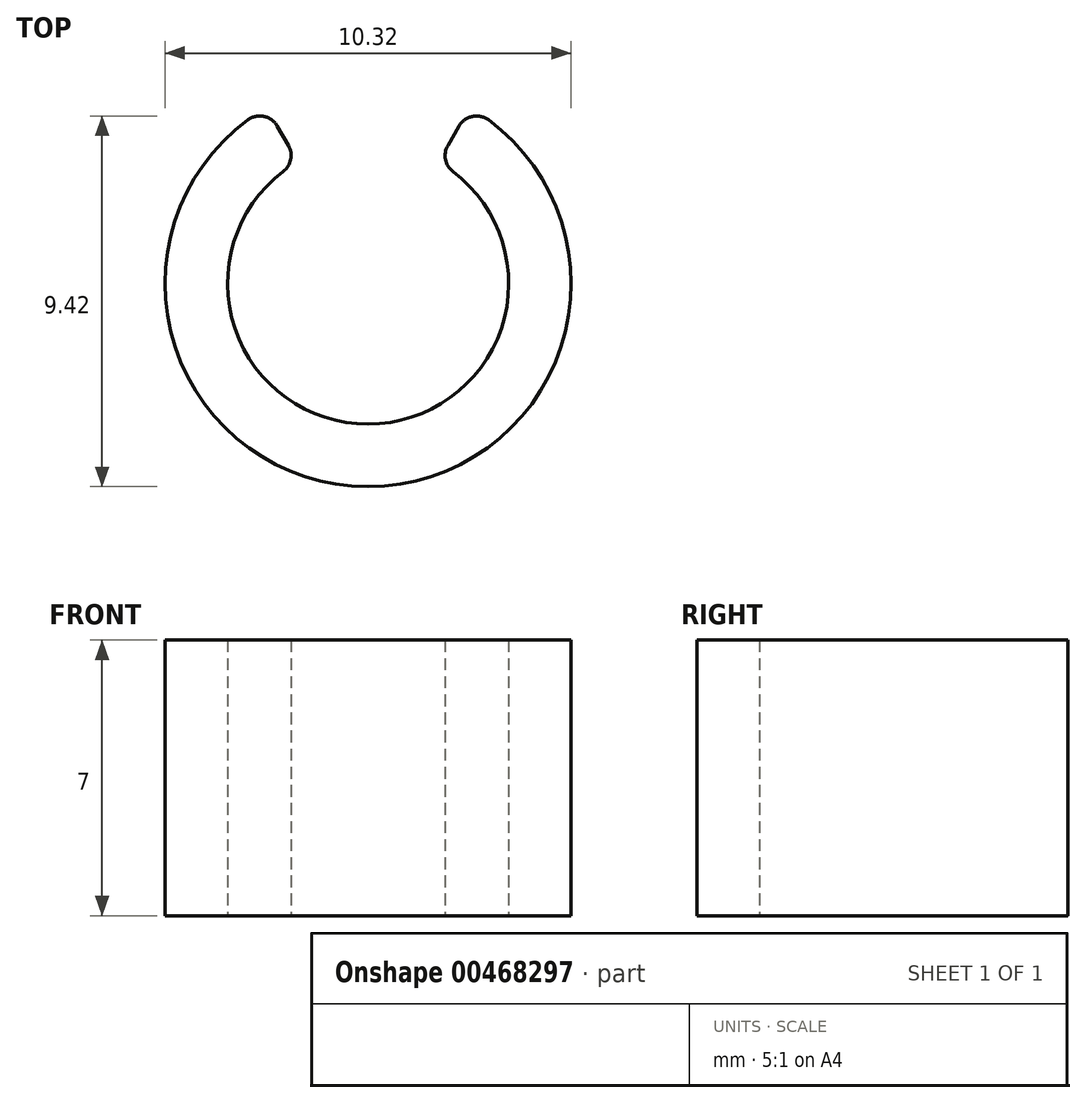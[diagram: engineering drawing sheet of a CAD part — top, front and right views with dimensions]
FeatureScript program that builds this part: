
annotation { "Feature Type Name" : "Feature", "Feature Type Description" : "" }
export const myFeature = defineFeature(function(context is Context, id is Id, definition is map)
    precondition{}
    {
        {
            var Q0;
            Q0=qCreatedBy(makeId("Top.planeOp"),FACE);
            var sketch = newSketch(context, id + "F0", { "sketchPlane" : qUnion([Q0])});
            skCircle(sketch, "E0", {"center": v(0, 0) * mm, "radius": 3.57 * mm});
            skCircle(sketch, "E1", {"center": v(0, 0) * mm, "radius": 5.16 * mm});
            skSolve(sketch);
        }
        {
            var Q0;
            Q0 = qSketchRegion(id + "F0", true);
            extrude(context, id + "F1", {"entities" : qUnion([Q0]), "depth" : 7 * mm});
        }
        {
            var Q0;
            Q0=qCreatedBy(makeId("Top.planeOp"),FACE);
            var sketch = newSketch(context, id + "F2", { "sketchPlane" : qUnion([Q0])});
            skCircle(sketch, "E2.cCircle", {"center": v(0, 3.44) * mm, "radius": 1.72 * mm, "construction": true});
            skLineSegment(sketch, "E2.0", {"start": v(0, 0) * mm, "end": v(-2.98, 5.16) * mm});
            skLineSegment(sketch, "E2.1", {"start": v(-2.98, 5.16) * mm, "end": v(2.98, 5.16) * mm});
            skLineSegment(sketch, "E2.2", {"start": v(2.98, 5.16) * mm, "end": v(0, 0) * mm});
            skPoint(sketch, "E2.0.midPoint", {"position": v(-1.49, 2.58) * mm});
            skSolve(sketch);
        }
        {
            var Q0;
            Q0 = qSketchRegion(id + "F2", true);
            extrude(context, id + "F3", {"entities" : qUnion([Q0]), "operationType" : NewBodyOperationType.REMOVE, "endBound" : BoundingType.THROUGH_ALL, "depth" : 25.4 * mm});
        }
        {
            var Q0;
            Q0=makeQuery(id+"F3.boolean.opBoolean","INTERSECT",EDGE,{"derivedFrom":[makeQuery(id+"F1.opExtrude","SWEPT_FACE",FACE,{"disambiguationData":[OSD([sQuery(id+"F0.wireOp",EDGE,"E0")])]}),makeQuery(id+"F3.opExtrude","SWEPT_FACE",FACE,{"disambiguationData":[OSD([sQuery(id+"F2.wireOp",EDGE,"E2.2")])]})]});
            var Q1;
            Q1=makeQuery(id+"F3.boolean.opBoolean","INTERSECT",EDGE,{"derivedFrom":[makeQuery(id+"F1.opExtrude","SWEPT_FACE",FACE,{"disambiguationData":[OSD([sQuery(id+"F0.wireOp",EDGE,"E0")])]}),makeQuery(id+"F3.opExtrude","SWEPT_FACE",FACE,{"disambiguationData":[OSD([sQuery(id+"F2.wireOp",EDGE,"E2.0")])]})]});
            var Q2;
            Q2=makeQuery(id+"F3.boolean.opBoolean","INTERSECT",EDGE,{"derivedFrom":[makeQuery(id+"F1.opExtrude","SWEPT_FACE",FACE,{"disambiguationData":[OSD([sQuery(id+"F0.wireOp",EDGE,"E1")])]}),makeQuery(id+"F3.opExtrude","SWEPT_FACE",FACE,{"disambiguationData":[OSD([sQuery(id+"F2.wireOp",EDGE,"E2.0")])]})]});
            var Q3;
            Q3=makeQuery(id+"F3.boolean.opBoolean","INTERSECT",EDGE,{"derivedFrom":[makeQuery(id+"F1.opExtrude","SWEPT_FACE",FACE,{"disambiguationData":[OSD([sQuery(id+"F0.wireOp",EDGE,"E1")])]}),makeQuery(id+"F3.opExtrude","SWEPT_FACE",FACE,{"disambiguationData":[OSD([sQuery(id+"F2.wireOp",EDGE,"E2.2")])]})]});
            fillet(context, id + "F4", {"entities" : qUnion([Q0, Q1, Q2, Q3]), "radius" : 0.5 * mm, "tangentPropagation" : true, "allowEdgeOverflow" : false});
        }
    });
